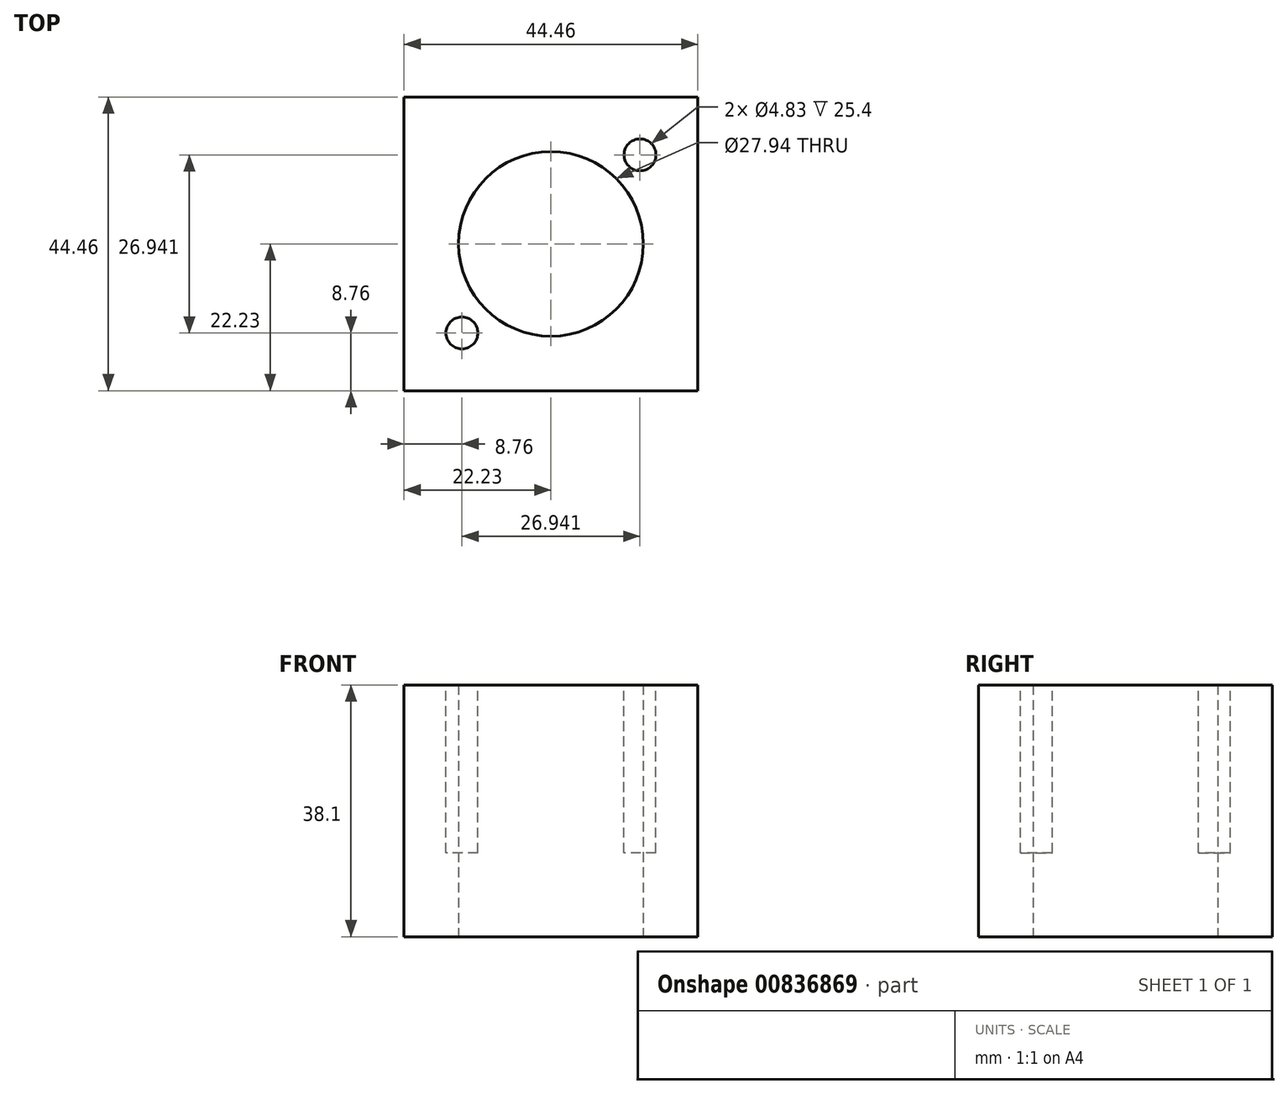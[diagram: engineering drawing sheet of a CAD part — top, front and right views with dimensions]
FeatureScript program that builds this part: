
annotation { "Feature Type Name" : "Feature", "Feature Type Description" : "" }
export const myFeature = defineFeature(function(context is Context, id is Id, definition is map)
    precondition{}
    {
        {
            var Q0;
            Q0=qCreatedBy(makeId("Top.planeOp"),FACE);
            var sketch = newSketch(context, id + "F0", { "sketchPlane" : qUnion([Q0])});
            skLineSegment(sketch, "E0.bottom", {"start": v(22.22, 22.23) * mm, "end": v(-22.23, 22.23) * mm});
            skLineSegment(sketch, "E0.top", {"start": v(22.23, -22.23) * mm, "end": v(-22.22, -22.23) * mm});
            skLineSegment(sketch, "E0.left", {"start": v(22.22, 22.23) * mm, "end": v(22.23, -22.23) * mm});
            skLineSegment(sketch, "E0.right", {"start": v(-22.23, 22.23) * mm, "end": v(-22.22, -22.23) * mm});
            skPoint(sketch, "E0.middle", {"position": v(0, 0) * mm});
            skCircle(sketch, "E1", {"center": v(0, 0) * mm, "radius": 13.97 * mm});
            skSolve(sketch);
        }
        {
            var Q0;
            Q0=makeQuery(id+"F0.imprint","IMPRINT",FACE,{"disambiguationData":[TD([[makeQuery(id+"F0.imprint","IMPRINT",EDGE,{"derivedFrom":sQuery(id+"F0.wireOp",EDGE,"E0.bottom")}),1.0]])]});
            extrude(context, id + "F1", {"entities" : qUnion([Q0]), "depth" : 38.1 * mm, "offsetDistance" : 25.4 * mm});
        }
        {
            var Q0;
            Q0=makeQuery(id+"F1.opExtrude","CAP_FACE",FACE,{"disambiguationData":[OSD([sQuery(id+"F0.wireOp",EDGE,"E0.bottom"),sQuery(id+"F0.wireOp",EDGE,"E0.top"),sQuery(id+"F0.wireOp",EDGE,"E0.left"),sQuery(id+"F0.wireOp",EDGE,"E0.right"),sQuery(id+"F0.wireOp",EDGE,"E1")])],"isStart":false});
            var sketch = newSketch(context, id + "F2", { "sketchPlane" : qUnion([Q0])});
            skLineSegment(sketch, "E2", {"start": v(-22.22, -22.22) * mm, "end": v(22.22, 22.22) * mm, "construction": true});
            skCircle(sketch, "E3", {"center": v(-13.47, -13.47) * mm, "radius": 2.41 * mm});
            skCircle(sketch, "E4", {"center": v(13.47, 13.47) * mm, "radius": 2.41 * mm});
            skPoint(sketch, "E5", {"position": v(0, 0) * mm});
            skSolve(sketch);
        }
        {
            var Q0;
            Q0 = qSketchRegion(id + "F2", true);
            extrude(context, id + "F3", {"entities" : qUnion([Q0]), "operationType" : NewBodyOperationType.REMOVE, "oppositeDirection" : true, "depth" : 25.4 * mm, "offsetDistance" : 25.4 * mm});
        }
    });
